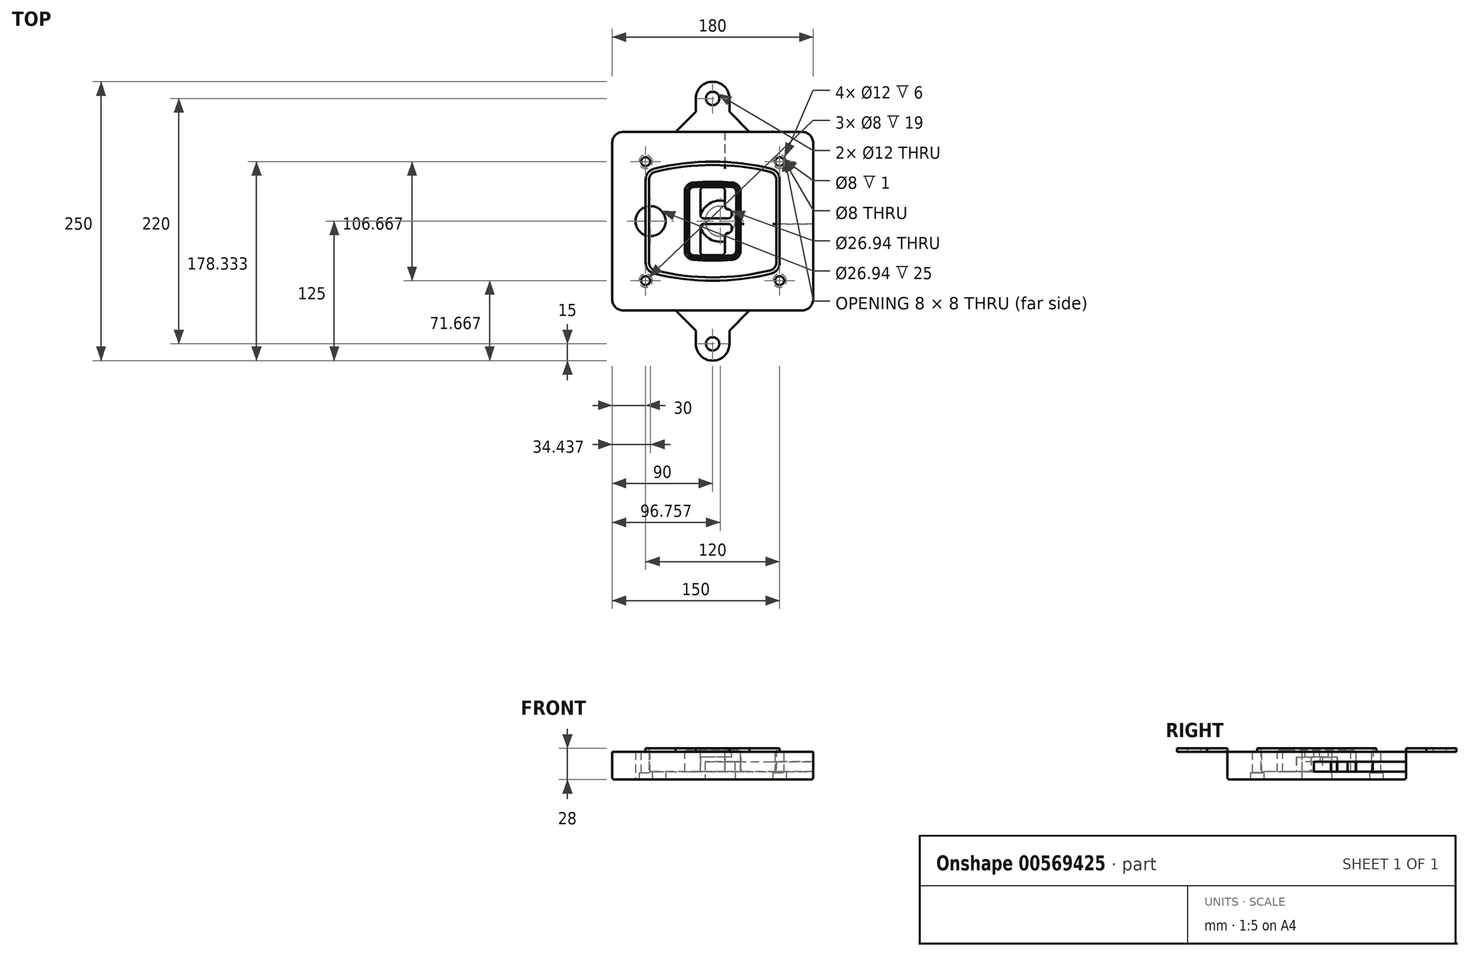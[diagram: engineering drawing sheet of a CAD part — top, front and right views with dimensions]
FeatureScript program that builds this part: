
annotation { "Feature Type Name" : "Feature", "Feature Type Description" : "" }
export const myFeature = defineFeature(function(context is Context, id is Id, definition is map)
    precondition{}
    {
        {
            var Q0;
            Q0=qCreatedBy(makeId("Top.planeOp"),FACE);
            var sketch = newSketch(context, id + "F0", { "sketchPlane" : qUnion([Q0])});
            skPoint(sketch, "E0.rect.middle", {"position": v(0, 0) * mm});
            skLineSegment(sketch, "E1.bottom", {"start": v(-80, -80) * mm, "end": v(80, -80) * mm});
            skLineSegment(sketch, "E1.top", {"start": v(-80, 80) * mm, "end": v(80, 80) * mm});
            skLineSegment(sketch, "E1.left", {"start": v(-90, -70) * mm, "end": v(-90, 70) * mm});
            skLineSegment(sketch, "E1.right", {"start": v(90, -70) * mm, "end": v(90, 70) * mm});
            skLineSegment(sketch, "E2", {"start": v(-90, 80) * mm, "end": v(90, -80) * mm, "construction": true});
            skLineSegment(sketch, "E3", {"start": v(90, 80) * mm, "end": v(-90, -80) * mm, "construction": true});
            skCircle(sketch, "E4", {"center": v(-60, 53.33) * mm, "radius": 4 * mm});
            skCircle(sketch, "E5", {"center": v(60, 53.33) * mm, "radius": 4 * mm});
            skCircle(sketch, "E6", {"center": v(60, -53.33) * mm, "radius": 4 * mm});
            skCircle(sketch, "E7", {"center": v(-60, -53.33) * mm, "radius": 4 * mm});
            skLineSegment(sketch, "E8", {"start": v(-60, 53.33) * mm, "end": v(60, 53.33) * mm, "construction": true});
            skLineSegment(sketch, "E9", {"start": v(60, 53.33) * mm, "end": v(60, -53.33) * mm, "construction": true});
            skLineSegment(sketch, "E10", {"start": v(60, -53.33) * mm, "end": v(-60, -53.33) * mm, "construction": true});
            skLineSegment(sketch, "E11", {"start": v(-60, -53.33) * mm, "end": v(-60, 53.33) * mm, "construction": true});
            skLineSegment(sketch, "E12", {"start": v(-60, 37.3) * mm, "end": v(-60, -37.3) * mm});
            skLineSegment(sketch, "E13", {"start": v(60, 37.3) * mm, "end": v(60, -37.3) * mm});
            skArc(sketch, "E14", {"start": v(52.38, 47.01) * mm, "mid": v(0, 53.33) * mm, "end": v(-52.38, 47.01) * mm});
            skArc(sketch, "E15", {"start": v(-52.38, -47.01) * mm, "mid": v(0, -53.33) * mm, "end": v(52.38, -47.01) * mm});
            skLineSegment(sketch, "E16", {"start": v(-60, 0) * mm, "end": v(60, 0) * mm, "construction": true});
            skPoint(sketch, "E17.visualSharp", {"position": v(-60, -45) * mm});
            skArc(sketch, "E17.filletArc", {"start": v(-60, -37.3) * mm, "mid": v(-57.87, -43.47) * mm, "end": v(-52.38, -47.01) * mm});
            skPoint(sketch, "E18.visualSharp", {"position": v(-60, 45) * mm});
            skArc(sketch, "E18.filletArc", {"start": v(-52.38, 47.01) * mm, "mid": v(-57.87, 43.47) * mm, "end": v(-60, 37.3) * mm});
            skPoint(sketch, "E19.visualSharp", {"position": v(60, 45) * mm});
            skArc(sketch, "E19.filletArc", {"start": v(60, 37.3) * mm, "mid": v(57.87, 43.47) * mm, "end": v(52.38, 47.01) * mm});
            skPoint(sketch, "E20.visualSharp", {"position": v(60, -45) * mm});
            skArc(sketch, "E20.filletArc", {"start": v(52.38, -47.01) * mm, "mid": v(57.87, -43.47) * mm, "end": v(60, -37.3) * mm});
            skPoint(sketch, "E21.visualSharp", {"position": v(-90, 80) * mm});
            skArc(sketch, "E21.filletArc", {"start": v(-80, 80) * mm, "mid": v(-87.07, 77.07) * mm, "end": v(-90, 70) * mm});
            skPoint(sketch, "E22.visualSharp", {"position": v(90, 80) * mm});
            skArc(sketch, "E22.filletArc", {"start": v(90, 70) * mm, "mid": v(87.07, 77.07) * mm, "end": v(80, 80) * mm});
            skPoint(sketch, "E23.visualSharp", {"position": v(90, -80) * mm});
            skArc(sketch, "E23.filletArc", {"start": v(80, -80) * mm, "mid": v(87.07, -77.07) * mm, "end": v(90, -70) * mm});
            skPoint(sketch, "E24.visualSharp", {"position": v(-90, -80) * mm});
            skArc(sketch, "E24.filletArc", {"start": v(-90, -70) * mm, "mid": v(-87.07, -77.07) * mm, "end": v(-80, -80) * mm});
            skArc(sketch, "E25.0", {"start": v(57, 37.3) * mm, "mid": v(55.5, 41.62) * mm, "end": v(51.67, 44.1) * mm});
            skLineSegment(sketch, "E25.1", {"start": v(57, 37.3) * mm, "end": v(57, -37.3) * mm});
            skArc(sketch, "E25.2", {"start": v(51.67, -44.1) * mm, "mid": v(55.5, -41.62) * mm, "end": v(57, -37.3) * mm});
            skArc(sketch, "E25.3", {"start": v(-51.67, -44.1) * mm, "mid": v(0, -50.33) * mm, "end": v(51.67, -44.1) * mm});
            skArc(sketch, "E25.4", {"start": v(-57, -37.3) * mm, "mid": v(-55.5, -41.62) * mm, "end": v(-51.67, -44.1) * mm});
            skArc(sketch, "E25.5", {"start": v(51.67, 44.1) * mm, "mid": v(0, 50.33) * mm, "end": v(-51.67, 44.1) * mm});
            skLineSegment(sketch, "E25.6", {"start": v(-57, 37.3) * mm, "end": v(-57, -37.3) * mm});
            skArc(sketch, "E25.7", {"start": v(-51.67, 44.1) * mm, "mid": v(-55.5, 41.62) * mm, "end": v(-57, 37.3) * mm});
            skArc(sketch, "E26.0", {"start": v(-53.33, 50.9) * mm, "mid": v(-61.01, 45.94) * mm, "end": v(-64, 37.3) * mm});
            skArc(sketch, "E26.1", {"start": v(53.33, 50.9) * mm, "mid": v(0, 57.33) * mm, "end": v(-53.33, 50.9) * mm});
            skArc(sketch, "E26.2", {"start": v(64, 37.3) * mm, "mid": v(61.01, 45.94) * mm, "end": v(53.33, 50.9) * mm});
            skLineSegment(sketch, "E26.3", {"start": v(64, 37.3) * mm, "end": v(64, -37.3) * mm});
            skArc(sketch, "E26.4", {"start": v(53.33, -50.9) * mm, "mid": v(61.01, -45.94) * mm, "end": v(64, -37.3) * mm});
            skLineSegment(sketch, "E26.5", {"start": v(-64, 37.3) * mm, "end": v(-64, -37.3) * mm});
            skArc(sketch, "E26.6", {"start": v(-53.33, -50.9) * mm, "mid": v(0, -57.33) * mm, "end": v(53.33, -50.9) * mm});
            skArc(sketch, "E26.7", {"start": v(-64, -37.3) * mm, "mid": v(-61.01, -45.94) * mm, "end": v(-53.33, -50.9) * mm});
            skSolve(sketch);
        }
        {
            var Q0;
            Q0=makeQuery(id+"F0.imprint","IMPRINT",FACE,{"disambiguationData":[TD([[makeQuery(id+"F0.imprint","IMPRINT",EDGE,{"derivedFrom":sQuery(id+"F0.wireOp",EDGE,"E1.bottom")}),1.0]])]});
            var Q1;
            Q1=makeQuery(id+"F0.imprint","IMPRINT",FACE,{"disambiguationData":[TD([[makeQuery(id+"F0.imprint","IMPRINT",EDGE,{"derivedFrom":sQuery(id+"F0.wireOp",EDGE,"E12")}),1.0]])]});
            var Q2;
            Q2=makeQuery(id+"F0.imprint","IMPRINT",FACE,{"disambiguationData":[TD([[makeQuery(id+"F0.imprint","IMPRINT",EDGE,{"derivedFrom":sQuery(id+"F0.wireOp",EDGE,"E25.0")}),1.0]])]});
            var Q3;
            Q3=makeQuery(id+"F0.imprint","IMPRINT",FACE,{"disambiguationData":[TD([[makeQuery(id+"F0.imprint","IMPRINT",EDGE,{"derivedFrom":sQuery(id+"F0.wireOp",EDGE,"E12")}),-1.0]])]});
            extrude(context, id + "F1", {"entities" : qUnion([Q0, Q1, Q2, Q3]), "oppositeDirection" : true, "depth" : 25 * mm});
        }
        {
            var Q0;
            Q0=makeQuery(id+"F0.imprint","IMPRINT",FACE,{"disambiguationData":[TD([[makeQuery(id+"F0.imprint","IMPRINT",EDGE,{"derivedFrom":sQuery(id+"F0.wireOp",EDGE,"E12")}),1.0]])]});
            extrude(context, id + "F2", {"entities" : qUnion([Q0]), "operationType" : NewBodyOperationType.ADD, "depth" : 3 * mm});
        }
        {
            var Q0;
            Q0=makeQuery(id+"F0.imprint","IMPRINT",FACE,{"disambiguationData":[TD([[makeQuery(id+"F0.imprint","IMPRINT",EDGE,{"derivedFrom":sQuery(id+"F0.wireOp",EDGE,"E25.0")}),1.0]])]});
            extrude(context, id + "F3", {"entities" : qUnion([Q0]), "operationType" : NewBodyOperationType.REMOVE, "oppositeDirection" : true, "depth" : 18 * mm});
        }
        {
            var Q0;
            Q0=makeQuery(id+"F2.opExtrude","CAP_FACE",FACE,{"disambiguationData":[OSD([sQuery(id+"F0.wireOp",EDGE,"E12"),sQuery(id+"F0.wireOp",EDGE,"E13"),sQuery(id+"F0.wireOp",EDGE,"E14"),sQuery(id+"F0.wireOp",EDGE,"E15"),sQuery(id+"F0.wireOp",EDGE,"E17.filletArc"),sQuery(id+"F0.wireOp",EDGE,"E18.filletArc"),sQuery(id+"F0.wireOp",EDGE,"E19.filletArc"),sQuery(id+"F0.wireOp",EDGE,"E20.filletArc"),sQuery(id+"F0.wireOp",EDGE,"E25.0"),sQuery(id+"F0.wireOp",EDGE,"E25.1"),sQuery(id+"F0.wireOp",EDGE,"E25.2"),sQuery(id+"F0.wireOp",EDGE,"E25.3"),sQuery(id+"F0.wireOp",EDGE,"E25.4"),sQuery(id+"F0.wireOp",EDGE,"E25.5"),sQuery(id+"F0.wireOp",EDGE,"E25.6"),sQuery(id+"F0.wireOp",EDGE,"E25.7")])],"isStart":false});
            var sketch = newSketch(context, id + "F4", { "sketchPlane" : qUnion([Q0])});
            skArc(sketch, "E27.0", {"start": v(-17.7, -34.56) * mm, "mid": v(0, -35.33) * mm, "end": v(17.7, -34.56) * mm});
            skArc(sketch, "E28.0", {"start": v(17.7, 34.56) * mm, "mid": v(0, 35.33) * mm, "end": v(-17.7, 34.56) * mm});
            skLineSegment(sketch, "E29", {"start": v(-25, 26.59) * mm, "end": v(-25, -26.59) * mm});
            skLineSegment(sketch, "E30", {"start": v(25, 26.59) * mm, "end": v(25, -26.59) * mm});
            skLineSegment(sketch, "E31", {"start": v(-25, 33.78) * mm, "end": v(25, 33.78) * mm, "construction": true});
            skLineSegment(sketch, "E32", {"start": v(-25, -33.78) * mm, "end": v(25, -33.78) * mm, "construction": true});
            skPoint(sketch, "E33.visualSharp", {"position": v(-25, 33.78) * mm});
            skArc(sketch, "E33.filletArc", {"start": v(-17.7, 34.56) * mm, "mid": v(-22.9, 32) * mm, "end": v(-25, 26.59) * mm});
            skPoint(sketch, "E34.visualSharp", {"position": v(25, 33.78) * mm});
            skArc(sketch, "E34.filletArc", {"start": v(25, 26.59) * mm, "mid": v(22.9, 32) * mm, "end": v(17.7, 34.56) * mm});
            skPoint(sketch, "E35.visualSharp", {"position": v(25, -33.78) * mm});
            skArc(sketch, "E35.filletArc", {"start": v(17.7, -34.56) * mm, "mid": v(22.9, -32) * mm, "end": v(25, -26.59) * mm});
            skPoint(sketch, "E36.visualSharp", {"position": v(-25, -33.78) * mm});
            skArc(sketch, "E36.filletArc", {"start": v(-25, -26.59) * mm, "mid": v(-22.9, -32) * mm, "end": v(-17.7, -34.56) * mm});
            skArc(sketch, "E37.0", {"start": v(51.67, 44.1) * mm, "mid": v(0, 50.33) * mm, "end": v(-51.67, 44.1) * mm});
            skArc(sketch, "E37.1", {"start": v(-51.67, 44.1) * mm, "mid": v(-55.5, 41.62) * mm, "end": v(-57, 37.3) * mm});
            skLineSegment(sketch, "E37.2", {"start": v(-57, 37.3) * mm, "end": v(-57, -37.3) * mm});
            skArc(sketch, "E37.3", {"start": v(-57, -37.3) * mm, "mid": v(-55.5, -41.62) * mm, "end": v(-51.67, -44.1) * mm});
            skArc(sketch, "E37.4", {"start": v(-51.67, -44.1) * mm, "mid": v(0, -50.33) * mm, "end": v(51.67, -44.1) * mm});
            skArc(sketch, "E37.5", {"start": v(51.67, -44.1) * mm, "mid": v(55.5, -41.62) * mm, "end": v(57, -37.3) * mm});
            skLineSegment(sketch, "E37.6", {"start": v(57, 37.3) * mm, "end": v(57, -37.3) * mm});
            skArc(sketch, "E37.7", {"start": v(57, 37.3) * mm, "mid": v(55.5, 41.62) * mm, "end": v(51.67, 44.1) * mm});
            skLineSegment(sketch, "E38.0", {"start": v(23, 26.59) * mm, "end": v(23, -26.59) * mm});
            skArc(sketch, "E38.1", {"start": v(17.53, -32.56) * mm, "mid": v(21.42, -30.64) * mm, "end": v(23, -26.59) * mm});
            skArc(sketch, "E38.2", {"start": v(-17.53, -32.56) * mm, "mid": v(0, -33.33) * mm, "end": v(17.53, -32.56) * mm});
            skArc(sketch, "E38.3", {"start": v(-23, -26.59) * mm, "mid": v(-21.42, -30.64) * mm, "end": v(-17.53, -32.56) * mm});
            skLineSegment(sketch, "E38.4", {"start": v(-23, 26.59) * mm, "end": v(-23, -26.59) * mm});
            skArc(sketch, "E38.5", {"start": v(23, 26.59) * mm, "mid": v(21.42, 30.64) * mm, "end": v(17.53, 32.56) * mm});
            skArc(sketch, "E38.6", {"start": v(-17.53, 32.56) * mm, "mid": v(-21.42, 30.64) * mm, "end": v(-23, 26.59) * mm});
            skArc(sketch, "E38.7", {"start": v(17.53, 32.56) * mm, "mid": v(0, 33.33) * mm, "end": v(-17.53, 32.56) * mm});
            skArc(sketch, "E39.0", {"start": v(21, 26.59) * mm, "mid": v(19.95, 29.29) * mm, "end": v(17.35, 30.57) * mm});
            skLineSegment(sketch, "E39.1", {"start": v(21, 26.59) * mm, "end": v(21, -26.59) * mm});
            skArc(sketch, "E39.2", {"start": v(17.35, -30.57) * mm, "mid": v(19.95, -29.29) * mm, "end": v(21, -26.59) * mm});
            skArc(sketch, "E39.3", {"start": v(-17.35, -30.57) * mm, "mid": v(0, -31.33) * mm, "end": v(17.35, -30.57) * mm});
            skArc(sketch, "E39.4", {"start": v(-21, -26.59) * mm, "mid": v(-19.95, -29.29) * mm, "end": v(-17.35, -30.57) * mm});
            skArc(sketch, "E39.5", {"start": v(17.35, 30.57) * mm, "mid": v(0, 31.33) * mm, "end": v(-17.35, 30.57) * mm});
            skLineSegment(sketch, "E39.6", {"start": v(-21, 26.59) * mm, "end": v(-21, -26.59) * mm});
            skArc(sketch, "E39.7", {"start": v(-17.35, 30.57) * mm, "mid": v(-19.95, 29.29) * mm, "end": v(-21, 26.59) * mm});
            skLineSegment(sketch, "E40", {"start": v(-25, 0) * mm, "end": v(25, 0) * mm, "construction": true});
            skLineSegment(sketch, "E41", {"start": v(-11, 5.5) * mm, "end": v(-11, 27.5) * mm});
            skLineSegment(sketch, "E42", {"start": v(-8, 30.5) * mm, "end": v(8, 30.5) * mm});
            skLineSegment(sketch, "E43", {"start": v(11, 27.5) * mm, "end": v(11, 13.5) * mm});
            skLineSegment(sketch, "E44", {"start": v(14, 10.5) * mm, "end": v(14, 10.5) * mm});
            skLineSegment(sketch, "E45", {"start": v(17, 7.5) * mm, "end": v(17, 5.5) * mm});
            skLineSegment(sketch, "E46", {"start": v(14, 2.5) * mm, "end": v(-8, 2.5) * mm});
            skPoint(sketch, "E47.visualSharp", {"position": v(-11, 30.5) * mm});
            skArc(sketch, "E47.filletArc", {"start": v(-8, 30.5) * mm, "mid": v(-10.12, 29.62) * mm, "end": v(-11, 27.5) * mm});
            skPoint(sketch, "E48.visualSharp", {"position": v(11, 30.5) * mm});
            skArc(sketch, "E48.filletArc", {"start": v(11, 27.5) * mm, "mid": v(10.12, 29.62) * mm, "end": v(8, 30.5) * mm});
            skPoint(sketch, "E49.visualSharp", {"position": v(11, 10.5) * mm});
            skArc(sketch, "E49.filletArc", {"start": v(11, 13.5) * mm, "mid": v(11.88, 11.38) * mm, "end": v(14, 10.5) * mm});
            skPoint(sketch, "E50.visualSharp", {"position": v(17, 10.5) * mm});
            skArc(sketch, "E50.filletArc", {"start": v(17, 7.5) * mm, "mid": v(16.12, 9.62) * mm, "end": v(14, 10.5) * mm});
            skPoint(sketch, "E51.visualSharp", {"position": v(17, 2.5) * mm});
            skArc(sketch, "E51.filletArc", {"start": v(14, 2.5) * mm, "mid": v(16.12, 3.38) * mm, "end": v(17, 5.5) * mm});
            skPoint(sketch, "E52.visualSharp", {"position": v(-11, 2.5) * mm});
            skArc(sketch, "E52.filletArc", {"start": v(-11, 5.5) * mm, "mid": v(-10.12, 3.38) * mm, "end": v(-8, 2.5) * mm});
            skLineSegment(sketch, "E53.0.MirrorCS", {"start": v(14, -2.5) * mm, "end": v(-8, -2.5) * mm});
            skArc(sketch, "E54.0.MirrorCS", {"start": v(-11, -5.5) * mm, "mid": v(-10.12, -3.38) * mm, "end": v(-8, -2.5) * mm});
            skLineSegment(sketch, "E55.0.MirrorCS", {"start": v(-11, -5.5) * mm, "end": v(-11, -27.5) * mm});
            skArc(sketch, "E56.0.MirrorCS", {"start": v(-8, -30.5) * mm, "mid": v(-10.12, -29.62) * mm, "end": v(-11, -27.5) * mm});
            skLineSegment(sketch, "E57.0.MirrorCS", {"start": v(-8, -30.5) * mm, "end": v(8, -30.5) * mm});
            skArc(sketch, "E58.0.MirrorCS", {"start": v(11, -27.5) * mm, "mid": v(10.12, -29.62) * mm, "end": v(8, -30.5) * mm});
            skLineSegment(sketch, "E59.0.MirrorCS", {"start": v(11, -27.5) * mm, "end": v(11, -13.5) * mm});
            skArc(sketch, "E60.0.MirrorCS", {"start": v(11, -13.5) * mm, "mid": v(11.88, -11.38) * mm, "end": v(14, -10.5) * mm});
            skArc(sketch, "E61.0.MirrorCS", {"start": v(17, -7.5) * mm, "mid": v(16.12, -9.62) * mm, "end": v(14, -10.5) * mm});
            skLineSegment(sketch, "E62.0.MirrorCS", {"start": v(17, -7.5) * mm, "end": v(17, -5.5) * mm});
            skArc(sketch, "E63.0.MirrorCS", {"start": v(14, -2.5) * mm, "mid": v(16.12, -3.38) * mm, "end": v(17, -5.5) * mm});
            skSolve(sketch);
        }
        {
            var Q0;
            Q0=makeQuery(id+"F4.imprint","IMPRINT",FACE,{"disambiguationData":[TD([[makeQuery(id+"F4.imprint","IMPRINT",EDGE,{"derivedFrom":sQuery(id+"F4.wireOp",EDGE,"E27.0")}),1.0]])]});
            var Q1;
            Q1=makeQuery(id+"F4.imprint","IMPRINT",FACE,{"disambiguationData":[TD([[makeQuery(id+"F4.imprint","IMPRINT",EDGE,{"derivedFrom":sQuery(id+"F4.wireOp",EDGE,"E38.0")}),-1.0]])]});
            var Q2;
            Q2=makeQuery(id+"F4.imprint","IMPRINT",FACE,{"disambiguationData":[TD([[makeQuery(id+"F4.imprint","IMPRINT",EDGE,{"derivedFrom":sQuery(id+"F4.wireOp",EDGE,"E39.0")}),1.0]])]});
            extrude(context, id + "F5", {"entities" : qUnion([Q0, Q1, Q2]), "operationType" : NewBodyOperationType.ADD, "endBound" : BoundingType.UP_TO_NEXT, "oppositeDirection" : true, "depth" : 25 * mm});
        }
        {
            var Q0;
            Q0=makeQuery(id+"F4.imprint","IMPRINT",FACE,{"disambiguationData":[TD([[makeQuery(id+"F4.imprint","IMPRINT",EDGE,{"derivedFrom":sQuery(id+"F4.wireOp",EDGE,"E38.0")}),-1.0]])]});
            extrude(context, id + "F6", {"entities" : qUnion([Q0]), "operationType" : NewBodyOperationType.REMOVE, "oppositeDirection" : true, "depth" : 2 * mm});
        }
        {
            var Q0;
            Q0=makeQuery(id+"F1.opExtrude","CAP_FACE",FACE,{"disambiguationData":[OSD([sQuery(id+"F0.wireOp",EDGE,"E1.bottom"),sQuery(id+"F0.wireOp",EDGE,"E1.top"),sQuery(id+"F0.wireOp",EDGE,"E1.left"),sQuery(id+"F0.wireOp",EDGE,"E1.right"),sQuery(id+"F0.wireOp",EDGE,"E4"),sQuery(id+"F0.wireOp",EDGE,"E5"),sQuery(id+"F0.wireOp",EDGE,"E6"),sQuery(id+"F0.wireOp",EDGE,"E7"),sQuery(id+"F0.wireOp",EDGE,"E21.filletArc"),sQuery(id+"F0.wireOp",EDGE,"E22.filletArc"),sQuery(id+"F0.wireOp",EDGE,"E23.filletArc"),sQuery(id+"F0.wireOp",EDGE,"E24.filletArc")])],"isStart":false});
            var sketch = newSketch(context, id + "F7", { "sketchPlane" : qUnion([Q0])});
            skCircle(sketch, "E64", {"center": v(6.76, 0) * mm, "radius": 13.47 * mm});
            skCircle(sketch, "E65", {"center": v(-55.56, 0) * mm, "radius": 13.47 * mm});
            skLineSegment(sketch, "E66", {"start": v(90, 0) * mm, "end": v(-90, 0) * mm});
            skCircle(sketch, "E67", {"center": v(6.76, 0) * mm, "radius": 18.47 * mm});
            skCircle(sketch, "E68", {"center": v(60, -53.33) * mm, "radius": 6 * mm});
            skCircle(sketch, "E69", {"center": v(-60, -53.33) * mm, "radius": 6 * mm});
            skCircle(sketch, "E70", {"center": v(-60, 53.33) * mm, "radius": 6 * mm});
            skCircle(sketch, "E71", {"center": v(60, 53.33) * mm, "radius": 6 * mm});
            skSolve(sketch);
        }
        {
            var Q0;
            {var subQ1=sQuery(id+"F7.wireOp",EDGE,"E66");var subQ4=sQuery(id+"F7.wireOp",EDGE,"E64");var subQ6=makeQuery(id+"F7.imprint","INTERSECT",VERTEX,{"disambiguationData":[OD(0.0)],"derivedFrom":[subQ4,subQ1]});Q0=makeQuery(id+"F7.imprint","IMPRINT",FACE,{"disambiguationData":[TD([[makeQuery(id+"F7.imprint","IMPRINT",EDGE,{"disambiguationData":[TD([[subQ6,-1.0]])],"derivedFrom":subQ4}),-1.0]])]});}
            var Q1;
            {var subQ0=sQuery(id+"F7.wireOp",EDGE,"E66");var subQ1=sQuery(id+"F7.wireOp",EDGE,"E64");var subQ3=makeQuery(id+"F7.imprint","INTERSECT",VERTEX,{"disambiguationData":[OD(0.0)],"derivedFrom":[subQ1,subQ0]});Q1=makeQuery(id+"F7.imprint","IMPRINT",FACE,{"disambiguationData":[TD([[makeQuery(id+"F7.imprint","IMPRINT",EDGE,{"disambiguationData":[TD([[subQ3,-1.0]])],"derivedFrom":subQ1}),1.0]])]});}
            var Q2;
            {var subQ0=sQuery(id+"F7.wireOp",EDGE,"E66");var subQ1=sQuery(id+"F7.wireOp",EDGE,"E64");var subQ3=makeQuery(id+"F7.imprint","INTERSECT",VERTEX,{"disambiguationData":[OD(0.0)],"derivedFrom":[subQ1,subQ0]});Q2=makeQuery(id+"F7.imprint","IMPRINT",FACE,{"disambiguationData":[TD([[makeQuery(id+"F7.imprint","IMPRINT",EDGE,{"disambiguationData":[TD([[subQ3,1.0]])],"derivedFrom":subQ1}),1.0]])]});}
            var Q3;
            {var subQ1=sQuery(id+"F7.wireOp",EDGE,"E66");var subQ4=sQuery(id+"F7.wireOp",EDGE,"E64");var subQ6=makeQuery(id+"F7.imprint","INTERSECT",VERTEX,{"disambiguationData":[OD(0.0)],"derivedFrom":[subQ4,subQ1]});Q3=makeQuery(id+"F7.imprint","IMPRINT",FACE,{"disambiguationData":[TD([[makeQuery(id+"F7.imprint","IMPRINT",EDGE,{"disambiguationData":[TD([[subQ6,1.0]])],"derivedFrom":subQ4}),-1.0]])]});}
            extrude(context, id + "F8", {"entities" : qUnion([Q0, Q1, Q2, Q3]), "operationType" : NewBodyOperationType.ADD, "oppositeDirection" : true, "depth" : 20 * mm});
        }
        {
            var Q0;
            {var subQ0=sQuery(id+"F7.wireOp",EDGE,"E66");var subQ1=sQuery(id+"F7.wireOp",EDGE,"E64");var subQ3=makeQuery(id+"F7.imprint","INTERSECT",VERTEX,{"disambiguationData":[OD(0.0)],"derivedFrom":[subQ1,subQ0]});Q0=makeQuery(id+"F7.imprint","IMPRINT",FACE,{"disambiguationData":[TD([[makeQuery(id+"F7.imprint","IMPRINT",EDGE,{"disambiguationData":[TD([[subQ3,-1.0]])],"derivedFrom":subQ1}),1.0]])]});}
            var Q1;
            {var subQ0=sQuery(id+"F7.wireOp",EDGE,"E66");var subQ1=sQuery(id+"F7.wireOp",EDGE,"E64");var subQ3=makeQuery(id+"F7.imprint","INTERSECT",VERTEX,{"disambiguationData":[OD(0.0)],"derivedFrom":[subQ1,subQ0]});Q1=makeQuery(id+"F7.imprint","IMPRINT",FACE,{"disambiguationData":[TD([[makeQuery(id+"F7.imprint","IMPRINT",EDGE,{"disambiguationData":[TD([[subQ3,1.0]])],"derivedFrom":subQ1}),1.0]])]});}
            extrude(context, id + "F9", {"entities" : qUnion([Q0, Q1]), "operationType" : NewBodyOperationType.REMOVE, "oppositeDirection" : true, "depth" : 16 * mm});
        }
        {
            var Q0;
            {var subQ0=sQuery(id+"F7.wireOp",EDGE,"E66");var subQ1=sQuery(id+"F7.wireOp",EDGE,"E65");var subQ3=makeQuery(id+"F7.imprint","INTERSECT",VERTEX,{"disambiguationData":[OD(0.0)],"derivedFrom":[subQ1,subQ0]});Q0=makeQuery(id+"F7.imprint","IMPRINT",FACE,{"disambiguationData":[TD([[makeQuery(id+"F7.imprint","IMPRINT",EDGE,{"disambiguationData":[TD([[subQ3,-1.0]])],"derivedFrom":subQ1}),1.0]])]});}
            var Q1;
            {var subQ0=sQuery(id+"F7.wireOp",EDGE,"E66");var subQ1=sQuery(id+"F7.wireOp",EDGE,"E65");var subQ3=makeQuery(id+"F7.imprint","INTERSECT",VERTEX,{"disambiguationData":[OD(0.0)],"derivedFrom":[subQ1,subQ0]});Q1=makeQuery(id+"F7.imprint","IMPRINT",FACE,{"disambiguationData":[TD([[makeQuery(id+"F7.imprint","IMPRINT",EDGE,{"disambiguationData":[TD([[subQ3,1.0]])],"derivedFrom":subQ1}),1.0]])]});}
            extrude(context, id + "F10", {"entities" : qUnion([Q0, Q1]), "operationType" : NewBodyOperationType.REMOVE, "oppositeDirection" : true, "depth" : 25 * mm});
        }
        {
            var Q0;
            Q0=makeQuery(id+"F7.imprint","IMPRINT",FACE,{"disambiguationData":[TD([[makeQuery(id+"F7.imprint","IMPRINT",EDGE,{"derivedFrom":sQuery(id+"F7.wireOp",EDGE,"E68")}),1.0]])]});
            var Q1;
            Q1=makeQuery(id+"F7.imprint","IMPRINT",FACE,{"disambiguationData":[TD([[makeQuery(id+"F7.imprint","IMPRINT",EDGE,{"derivedFrom":makeQuery(id+"F1.opExtrude","CAP_EDGE",EDGE,{"disambiguationData":[OSD([sQuery(id+"F0.wireOp",EDGE,"E5")])],"isStart":false})}),-1.0]])]});
            var Q2;
            Q2=makeQuery(id+"F7.imprint","IMPRINT",FACE,{"disambiguationData":[TD([[makeQuery(id+"F7.imprint","IMPRINT",EDGE,{"derivedFrom":sQuery(id+"F7.wireOp",EDGE,"E69")}),1.0]])]});
            var Q3;
            Q3=makeQuery(id+"F7.imprint","IMPRINT",FACE,{"disambiguationData":[TD([[makeQuery(id+"F7.imprint","IMPRINT",EDGE,{"derivedFrom":makeQuery(id+"F1.opExtrude","CAP_EDGE",EDGE,{"disambiguationData":[OSD([sQuery(id+"F0.wireOp",EDGE,"E4")])],"isStart":false})}),-1.0]])]});
            var Q4;
            Q4=makeQuery(id+"F7.imprint","IMPRINT",FACE,{"disambiguationData":[TD([[makeQuery(id+"F7.imprint","IMPRINT",EDGE,{"derivedFrom":sQuery(id+"F7.wireOp",EDGE,"E70")}),1.0]])]});
            var Q5;
            Q5=makeQuery(id+"F7.imprint","IMPRINT",FACE,{"disambiguationData":[TD([[makeQuery(id+"F7.imprint","IMPRINT",EDGE,{"derivedFrom":makeQuery(id+"F1.opExtrude","CAP_EDGE",EDGE,{"disambiguationData":[OSD([sQuery(id+"F0.wireOp",EDGE,"E7")])],"isStart":false})}),-1.0]])]});
            var Q6;
            Q6=makeQuery(id+"F7.imprint","IMPRINT",FACE,{"disambiguationData":[TD([[makeQuery(id+"F7.imprint","IMPRINT",EDGE,{"derivedFrom":sQuery(id+"F7.wireOp",EDGE,"E71")}),1.0]])]});
            var Q7;
            Q7=makeQuery(id+"F7.imprint","IMPRINT",FACE,{"disambiguationData":[TD([[makeQuery(id+"F7.imprint","IMPRINT",EDGE,{"derivedFrom":makeQuery(id+"F1.opExtrude","CAP_EDGE",EDGE,{"disambiguationData":[OSD([sQuery(id+"F0.wireOp",EDGE,"E6")])],"isStart":false})}),-1.0]])]});
            extrude(context, id + "F11", {"entities" : qUnion([Q0, Q1, Q2, Q3, Q4, Q5, Q6, Q7]), "operationType" : NewBodyOperationType.REMOVE, "oppositeDirection" : true, "depth" : 6 * mm});
        }
        {
            var Q0;
            Q0=makeQuery(id+"F9.boolean.opBoolean","COPY",FACE,{"derivedFrom":makeQuery(id+"F9.opExtrude","CAP_FACE",FACE,{"disambiguationData":[OSD([sQuery(id+"F7.wireOp",EDGE,"E64")])],"isStart":false})});
            var sketch = newSketch(context, id + "F12", { "sketchPlane" : qUnion([Q0])});
            skArc(sketch, "E72.0", {"start": v(11, -88.19) * mm, "mid": v(97.1, -83.6) * mm, "end": v(92.5, 2.5) * mm});
            skLineSegment(sketch, "E72.1", {"start": v(11, -17.97) * mm, "end": v(11, -17.97) * mm});
            skLineSegment(sketch, "E73", {"start": v(92.5, -105.13) * mm, "end": v(102.3, -105.13) * mm});
            skLineSegment(sketch, "E74.0", {"start": v(92.5, 2.5) * mm, "end": v(14, 2.5) * mm});
            skArc(sketch, "E74.1", {"start": v(14, 2.5) * mm, "mid": v(16.12, 3.38) * mm, "end": v(17, 5.5) * mm});
            skLineSegment(sketch, "E74.2", {"start": v(17, 7.5) * mm, "end": v(17, 5.5) * mm});
            skArc(sketch, "E74.3", {"start": v(17, 7.5) * mm, "mid": v(16.12, 9.62) * mm, "end": v(14, 10.5) * mm});
            skArc(sketch, "E74.4", {"start": v(11, 13.5) * mm, "mid": v(11.88, 11.38) * mm, "end": v(14, 10.5) * mm});
            skLineSegment(sketch, "E74.5", {"start": v(11, 13.5) * mm, "end": v(11, -88.19) * mm});
            skLineSegment(sketch, "E74.7", {"start": v(92.5, -2.5) * mm, "end": v(14, -2.5) * mm});
            skArc(sketch, "E74.8", {"start": v(14, -2.5) * mm, "mid": v(16.12, -3.38) * mm, "end": v(17, -5.5) * mm});
            skLineSegment(sketch, "E74.9", {"start": v(17, -7.5) * mm, "end": v(17, -5.5) * mm});
            skArc(sketch, "E74.10", {"start": v(17, -7.5) * mm, "mid": v(16.12, -9.62) * mm, "end": v(14, -10.5) * mm});
            skArc(sketch, "E74.11", {"start": v(11, -13.5) * mm, "mid": v(11.88, -11.38) * mm, "end": v(14, -10.5) * mm});
            skLineSegment(sketch, "E74.12", {"start": v(11, -17.97) * mm, "end": v(11, -13.5) * mm});
            skPoint(sketch, "E75.orphan", {"position": v(11, -27.5) * mm});
            skPoint(sketch, "E76.orphan", {"position": v(-8, -2.5) * mm});
            skPoint(sketch, "E77.orphan", {"position": v(-8, 2.5) * mm});
            skPoint(sketch, "E78.orphan", {"position": v(11, 27.5) * mm});
            skSolve(sketch);
        }
        {
            var Q0;
            {var subQ7=sQuery(id+"F12.wireOp",EDGE,"E72.0");var subQ14=sQuery(id+"F12.wireOp",EDGE,"E72.1");var subQ16=sQuery(id+"F12.wireOp",EDGE,"E74.1");var subQ18=sQuery(id+"F12.wireOp",EDGE,"E74.8");Q0=qUnion([makeQuery(id+"F12.imprint","IMPRINT",FACE,{"disambiguationData":[TD([[makeQuery(id+"F12.imprint","IMPRINT",EDGE,{"derivedFrom":subQ7}),1.0]])]}),makeQuery(id+"F12.imprint","IMPRINT",FACE,{"disambiguationData":[TD([[makeQuery(id+"F12.imprint","IMPRINT",EDGE,{"derivedFrom":subQ14}),1.0]])]}),makeQuery(id+"F12.imprint","IMPRINT",FACE,{"disambiguationData":[TD([[makeQuery(id+"F12.imprint","IMPRINT",EDGE,{"derivedFrom":subQ16}),1.0]])]}),makeQuery(id+"F12.imprint","IMPRINT",FACE,{"disambiguationData":[TD([[makeQuery(id+"F12.imprint","IMPRINT",EDGE,{"derivedFrom":subQ18}),-1.0]])]})]);}
            var Q1;
            Q1=makeQuery(id+"F5.boolean.opBoolean","SPLIT",FACE,{"disambiguationData":[TD([makeQuery(id+"F5.opExtrude","SWEPT_FACE",FACE,{"disambiguationData":[OSD([sQuery(id+"F4.wireOp",EDGE,"E41")])]})])],"derivedFrom":makeQuery(id+"F3.boolean.opBoolean","COPY",FACE,{"derivedFrom":makeQuery(id+"F3.opExtrude","CAP_FACE",FACE,{"disambiguationData":[OSD([sQuery(id+"F0.wireOp",EDGE,"E25.0"),sQuery(id+"F0.wireOp",EDGE,"E25.1"),sQuery(id+"F0.wireOp",EDGE,"E25.2"),sQuery(id+"F0.wireOp",EDGE,"E25.3"),sQuery(id+"F0.wireOp",EDGE,"E25.4"),sQuery(id+"F0.wireOp",EDGE,"E25.5"),sQuery(id+"F0.wireOp",EDGE,"E25.6"),sQuery(id+"F0.wireOp",EDGE,"E25.7")])],"isStart":false})})});
            extrude(context, id + "F13", {"entities" : qUnion([Q0]), "operationType" : NewBodyOperationType.REMOVE, "endBound" : BoundingType.UP_TO_SURFACE, "endBoundEntityFace" : qUnion([Q1]), "depth" : 25 * mm});
        }
        {
            var Q0;
            Q0=makeQuery(id+"F3.boolean.opBoolean","COPY",EDGE,{"derivedFrom":makeQuery(id+"F3.opExtrude","CAP_EDGE",EDGE,{"disambiguationData":[OSD([sQuery(id+"F0.wireOp",EDGE,"E25.6")])],"isStart":false})});
            var Q1;
            Q1=makeQuery(id+"F8.boolean.opBoolean","INTERSECT",EDGE,{"derivedFrom":[makeQuery(id+"F5.opExtrude","SWEPT_FACE",FACE,{"disambiguationData":[OSD([sQuery(id+"F4.wireOp",EDGE,"E30")])]}),makeQuery(id+"F8.opExtrude","CAP_FACE",FACE,{"disambiguationData":[OSD([sQuery(id+"F7.wireOp",EDGE,"E67")])],"isStart":false})]});
            var Q2;
            Q2=makeQuery(id+"F8.boolean.opBoolean","INTERSECT",EDGE,{"disambiguationData":[OD(1.0)],"derivedFrom":[makeQuery(id+"F5.opExtrude","SWEPT_FACE",FACE,{"disambiguationData":[OSD([sQuery(id+"F4.wireOp",EDGE,"E30")])]}),makeQuery(id+"F8.opExtrude","SWEPT_FACE",FACE,{"disambiguationData":[OSD([sQuery(id+"F7.wireOp",EDGE,"E67")])]})]});
            var Q3;
            {var subQ0=makeQuery(id+"F3.boolean.opBoolean","COPY",FACE,{"derivedFrom":makeQuery(id+"F3.opExtrude","CAP_FACE",FACE,{"disambiguationData":[OSD([sQuery(id+"F0.wireOp",EDGE,"E25.0"),sQuery(id+"F0.wireOp",EDGE,"E25.1"),sQuery(id+"F0.wireOp",EDGE,"E25.2"),sQuery(id+"F0.wireOp",EDGE,"E25.3"),sQuery(id+"F0.wireOp",EDGE,"E25.4"),sQuery(id+"F0.wireOp",EDGE,"E25.5"),sQuery(id+"F0.wireOp",EDGE,"E25.6"),sQuery(id+"F0.wireOp",EDGE,"E25.7")])],"isStart":false})});var subQ1=sQuery(id+"F4.wireOp",EDGE,"E30");Q3=makeQuery(id+"F8.boolean.opBoolean","SPLIT",EDGE,{"disambiguationData":[TD([makeQuery(id+"F5.opExtrude","SWEPT_FACE",FACE,{"disambiguationData":[OSD([sQuery(id+"F4.wireOp",EDGE,"E35.filletArc")])]})])],"derivedFrom":makeQuery(id+"F5.opExtrude","TWEAK_EDGE",EDGE,{"derivedFrom":[subQ0,makeQuery(id+"F4.imprint","IMPRINT",EDGE,{"derivedFrom":subQ1})]})});}
            var Q4;
            {var subQ0=sQuery(id+"F0.wireOp",EDGE,"E25.0");var subQ1=sQuery(id+"F0.wireOp",EDGE,"E25.1");var subQ2=sQuery(id+"F0.wireOp",EDGE,"E25.2");var subQ3=sQuery(id+"F0.wireOp",EDGE,"E25.3");var subQ4=sQuery(id+"F0.wireOp",EDGE,"E25.4");var subQ5=sQuery(id+"F0.wireOp",EDGE,"E25.5");var subQ6=sQuery(id+"F0.wireOp",EDGE,"E25.6");var subQ7=sQuery(id+"F0.wireOp",EDGE,"E25.7");Q4=makeQuery(id+"F8.boolean.opBoolean","INTERSECT",EDGE,{"derivedFrom":[makeQuery(id+"F5.boolean.opBoolean","SPLIT",FACE,{"disambiguationData":[TD([makeQuery(id+"F2.opExtrude","SWEPT_FACE",FACE,{"disambiguationData":[OSD([subQ0])]})])],"derivedFrom":makeQuery(id+"F3.boolean.opBoolean","COPY",FACE,{"derivedFrom":makeQuery(id+"F3.opExtrude","CAP_FACE",FACE,{"disambiguationData":[OSD([subQ0,subQ1,subQ2,subQ3,subQ4,subQ5,subQ6,subQ7])],"isStart":false})})}),makeQuery(id+"F8.opExtrude","SWEPT_FACE",FACE,{"disambiguationData":[OSD([sQuery(id+"F7.wireOp",EDGE,"E67")])]})]});}
            var Q5;
            Q5=makeQuery(id+"F8.boolean.opBoolean","INTERSECT",EDGE,{"disambiguationData":[OD(0.0)],"derivedFrom":[makeQuery(id+"F5.opExtrude","SWEPT_FACE",FACE,{"disambiguationData":[OSD([sQuery(id+"F4.wireOp",EDGE,"E30")])]}),makeQuery(id+"F8.opExtrude","SWEPT_FACE",FACE,{"disambiguationData":[OSD([sQuery(id+"F7.wireOp",EDGE,"E67")])]})]});
            fillet(context, id + "F14", {"entities" : qUnion([Q0, Q1, Q2, Q3, Q4, Q5]), "radius" : 3 * mm, "tangentPropagation" : true, "allowEdgeOverflow" : false});
        }
        {
            var Q0;
            Q0=makeQuery(id+"F1.opExtrude","CAP_EDGE",EDGE,{"disambiguationData":[OSD([sQuery(id+"F0.wireOp",EDGE,"E1.bottom")])],"isStart":false});
            fillet(context, id + "F15", {"entities" : qUnion([Q0]), "radius" : 2 * mm, "tangentPropagation" : true, "allowEdgeOverflow" : false});
        }
        {
            var Q0;
            {var subQ0=sQuery(id+"F0.wireOp",EDGE,"E21.filletArc");var subQ1=sQuery(id+"F0.wireOp",EDGE,"E7");var subQ2=sQuery(id+"F0.wireOp",EDGE,"E6");var subQ3=sQuery(id+"F0.wireOp",EDGE,"E5");var subQ4=sQuery(id+"F0.wireOp",EDGE,"E4");var subQ5=sQuery(id+"F0.wireOp",EDGE,"E22.filletArc");var subQ6=sQuery(id+"F0.wireOp",EDGE,"E1.bottom");var subQ7=sQuery(id+"F0.wireOp",EDGE,"E1.right");var subQ8=sQuery(id+"F0.wireOp",EDGE,"E1.top");var subQ9=sQuery(id+"F0.wireOp",EDGE,"E1.left");var subQ10=sQuery(id+"F0.wireOp",EDGE,"E23.filletArc");var subQ11=sQuery(id+"F0.wireOp",EDGE,"E24.filletArc");Q0=makeQuery(id+"F2.boolean.opBoolean","SPLIT",FACE,{"disambiguationData":[TD([makeQuery(id+"F1.opExtrude","SWEPT_FACE",FACE,{"disambiguationData":[OSD([subQ6])]})])],"derivedFrom":makeQuery(id+"F1.opExtrude","CAP_FACE",FACE,{"disambiguationData":[OSD([subQ6,subQ8,subQ9,subQ7,subQ4,subQ3,subQ2,subQ1,subQ0,subQ5,subQ10,subQ11])],"isStart":true})});}
            var sketch = newSketch(context, id + "F16", { "sketchPlane" : qUnion([Q0])});
            skPoint(sketch, "E79.endSnap0", {"position": v(0, 80) * mm});
            skCircle(sketch, "E80", {"center": v(0, 110) * mm, "radius": 6 * mm});
            skArc(sketch, "E81", {"start": v(15, 110) * mm, "mid": v(0, 125) * mm, "end": v(-15, 110) * mm});
            skLineSegment(sketch, "E82", {"start": v(-15, 110) * mm, "end": v(-15, 98) * mm});
            skLineSegment(sketch, "E83", {"start": v(15, 110) * mm, "end": v(15, 98) * mm});
            skLineSegment(sketch, "E84", {"start": v(-15, 98) * mm, "end": v(-33, 80) * mm});
            skLineSegment(sketch, "E85", {"start": v(15, 98) * mm, "end": v(33, 80) * mm});
            skPoint(sketch, "E86.endSnap0", {"position": v(0, -53.33) * mm});
            skLineSegment(sketch, "E87", {"start": v(0, 110) * mm, "end": v(0, -89.13) * mm, "construction": true});
            skPoint(sketch, "E87.endSnap0", {"position": v(0, 53.33) * mm});
            skArc(sketch, "E88.MirrorCS", {"start": v(-15, 110) * mm, "mid": v(0, 125) * mm, "end": v(15, 110) * mm});
            skLineSegment(sketch, "E89", {"start": v(0, 0) * mm, "end": v(-117.12, 0) * mm});
            skPoint(sketch, "E89.endSnap0", {"position": v(-90, 0) * mm});
            skLineSegment(sketch, "E90.MirrorCS", {"start": v(-15, -98) * mm, "end": v(-33, -80) * mm});
            skLineSegment(sketch, "E91.MirrorCS", {"start": v(-15, -110) * mm, "end": v(-15, -98) * mm});
            skArc(sketch, "E92.MirrorCS", {"start": v(-15, -110) * mm, "mid": v(0, -125) * mm, "end": v(15, -110) * mm});
            skLineSegment(sketch, "E93.MirrorCS", {"start": v(15, -110) * mm, "end": v(15, -98) * mm});
            skLineSegment(sketch, "E94.MirrorCS", {"start": v(15, -98) * mm, "end": v(33, -80) * mm});
            skCircle(sketch, "E95.MirrorC", {"center": v(0, -110) * mm, "radius": 6 * mm});
            skSolve(sketch);
        }
        {
            var Q0;
            {var subQ1=sQuery(id+"F16.wireOp",EDGE,"E84");Q0=makeQuery(id+"F16.imprint","IMPRINT",FACE,{"disambiguationData":[TD([[makeQuery(id+"F16.imprint","IMPRINT",EDGE,{"derivedFrom":subQ1}),1.0]])]});}
            var Q1;
            {var subQ0=sQuery(id+"F16.wireOp",EDGE,"E90.MirrorCS");Q1=makeQuery(id+"F16.imprint","IMPRINT",FACE,{"disambiguationData":[TD([[makeQuery(id+"F16.imprint","IMPRINT",EDGE,{"derivedFrom":subQ0}),-1.0]])]});}
            var Q2;
            Q2=makeQuery(id+"F2.opExtrude","CAP_FACE",FACE,{"disambiguationData":[OSD([sQuery(id+"F0.wireOp",EDGE,"E12"),sQuery(id+"F0.wireOp",EDGE,"E13"),sQuery(id+"F0.wireOp",EDGE,"E14"),sQuery(id+"F0.wireOp",EDGE,"E15"),sQuery(id+"F0.wireOp",EDGE,"E17.filletArc"),sQuery(id+"F0.wireOp",EDGE,"E18.filletArc"),sQuery(id+"F0.wireOp",EDGE,"E19.filletArc"),sQuery(id+"F0.wireOp",EDGE,"E20.filletArc"),sQuery(id+"F0.wireOp",EDGE,"E25.0"),sQuery(id+"F0.wireOp",EDGE,"E25.1"),sQuery(id+"F0.wireOp",EDGE,"E25.2"),sQuery(id+"F0.wireOp",EDGE,"E25.3"),sQuery(id+"F0.wireOp",EDGE,"E25.4"),sQuery(id+"F0.wireOp",EDGE,"E25.5"),sQuery(id+"F0.wireOp",EDGE,"E25.6"),sQuery(id+"F0.wireOp",EDGE,"E25.7")])],"isStart":false});
            extrude(context, id + "F17", {"entities" : qUnion([Q0, Q1]), "endBound" : BoundingType.UP_TO_SURFACE, "depth" : 25 * mm, "endBoundEntityFace" : qUnion([Q2]), "offsetDistance" : 25 * mm});
        }
    });
